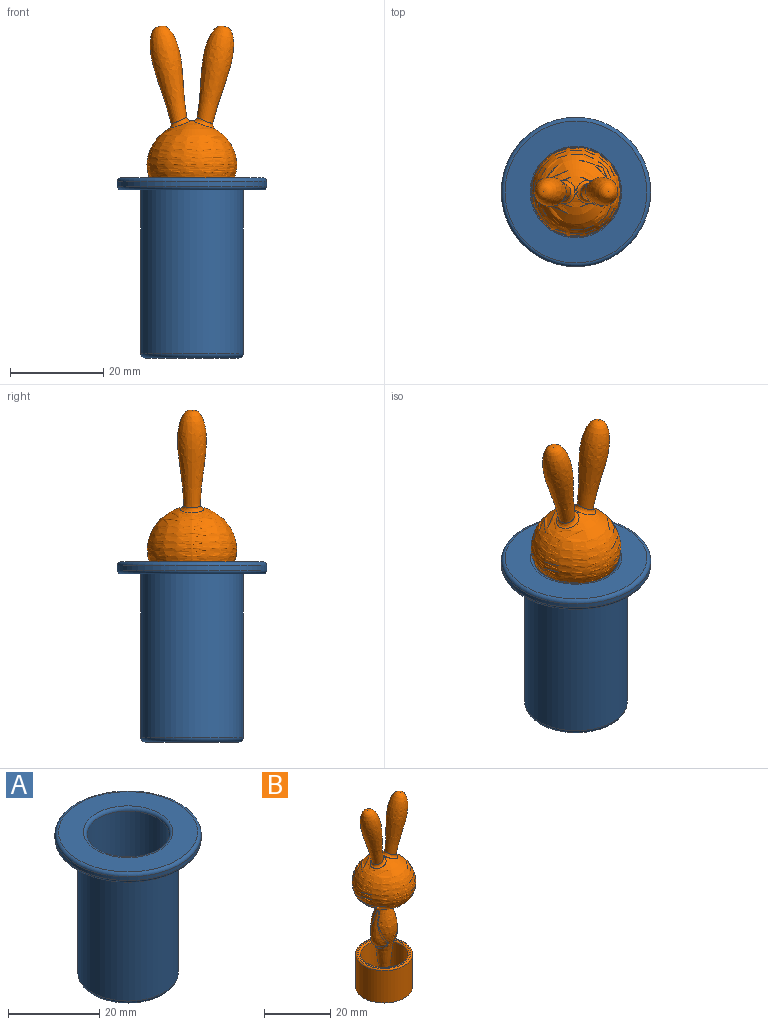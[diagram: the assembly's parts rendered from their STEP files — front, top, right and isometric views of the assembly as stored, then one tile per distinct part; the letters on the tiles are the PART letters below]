
ASSEMBLY  parts=2 mates=1
PART A: 11 faces, bbox 34.6x34.6x38.6 mm
  f0: cylinder r=9mm len=35.2mm, axis (0,0,1), area 1990.5mm2, adj f1,f9
  f1: plane 18x18mm, normal (0,0,1), area 254.5mm2, adj f0
  f2: plane 20x20mm, normal (0,0,-1), area 314.2mm2, adj f10
  f3: cylinder r=11mm len=35mm, axis (0,0,1), area 2419mm2, adj f4,f10
  f4: plane 30.4x30.4mm, normal (0,0,-1), area 345.7mm2, adj f3,f5
  f5: torus R=15.2mm, axis (0,0,1), area 124mm2, adj f4,f6
  f6: cylinder r=16mm len=32mm, axis (0,0,1), area 97.5mm2, adj f5,f7
  f7: torus R=15.2mm, axis (0,0,1), area 124mm2, adj f6,f8
  f8: plane 30.4x30.4mm, normal (0,0,1), area 424.1mm2, adj f7,f9
  f9: torus R=9.8mm, axis (0,0,1), area 73.4mm2, adj f0,f8
  f10: torus R=10mm, axis (0,0,1), area 105mm2, adj f2,f3
PART B: 16 faces, bbox 19.2x19.2x49 mm
  f0: bspline ~12.12x6.22mm, area 52.2mm2, adj f1
  f1: bspline ~13.72x6.23mm, area 18.4mm2, adj f0,f2
  f2: revolved ~46.33x19.18mm, area 1373.8mm2, adj f1,f3,f5,f7,f14
  f3: bspline ~13.72x6.23mm, area 18.4mm2, adj f2,f4
  f4: bspline ~15.04x13.85mm, area 52.3mm2, adj f3
  f5: bspline ~4.95x4.75mm, area 16.5mm2, adj f2,f6
  f6: revolved ~3.62x3.54mm, area 3.6mm2, adj f5
  f7: plane 14.26x14.26mm, normal (0,0,1), area 155.8mm2, adj f2,f8
  f8: cylinder r=7.13mm len=14.26mm, axis (0,0,1), area 450mm2, adj f7,f9
  f9: torus R=7.63mm, axis (0,0,1), area 36.1mm2, adj f8,f10
  f10: plane 16.22x16.22mm, normal (0,0,1), area 23.7mm2, adj f9,f11
  f11: torus R=8.11mm, axis (0,0,1), area 41.6mm2, adj f10,f12
  f12: cylinder r=8.61mm len=17.22mm, axis (0,0,1), area 644.2mm2, adj f11,f13
  f13: plane 17.22x17.22mm, normal (0,0,-1), area 232.9mm2, adj f12
  f14: bspline ~4.95x4.74mm, area 16.5mm2, adj f2,f15
  f15: revolved ~0.74x0.69mm, area 0mm2, adj f14
PLACE A t=(-14.05,4.7,2.51)mm
PLACE B t=(-14.05,4.7,2.51)mm
MATE slider B.f8 <-> A.f0  axis (0,0,-1) through (-14.05,4.7,2.51)mm
